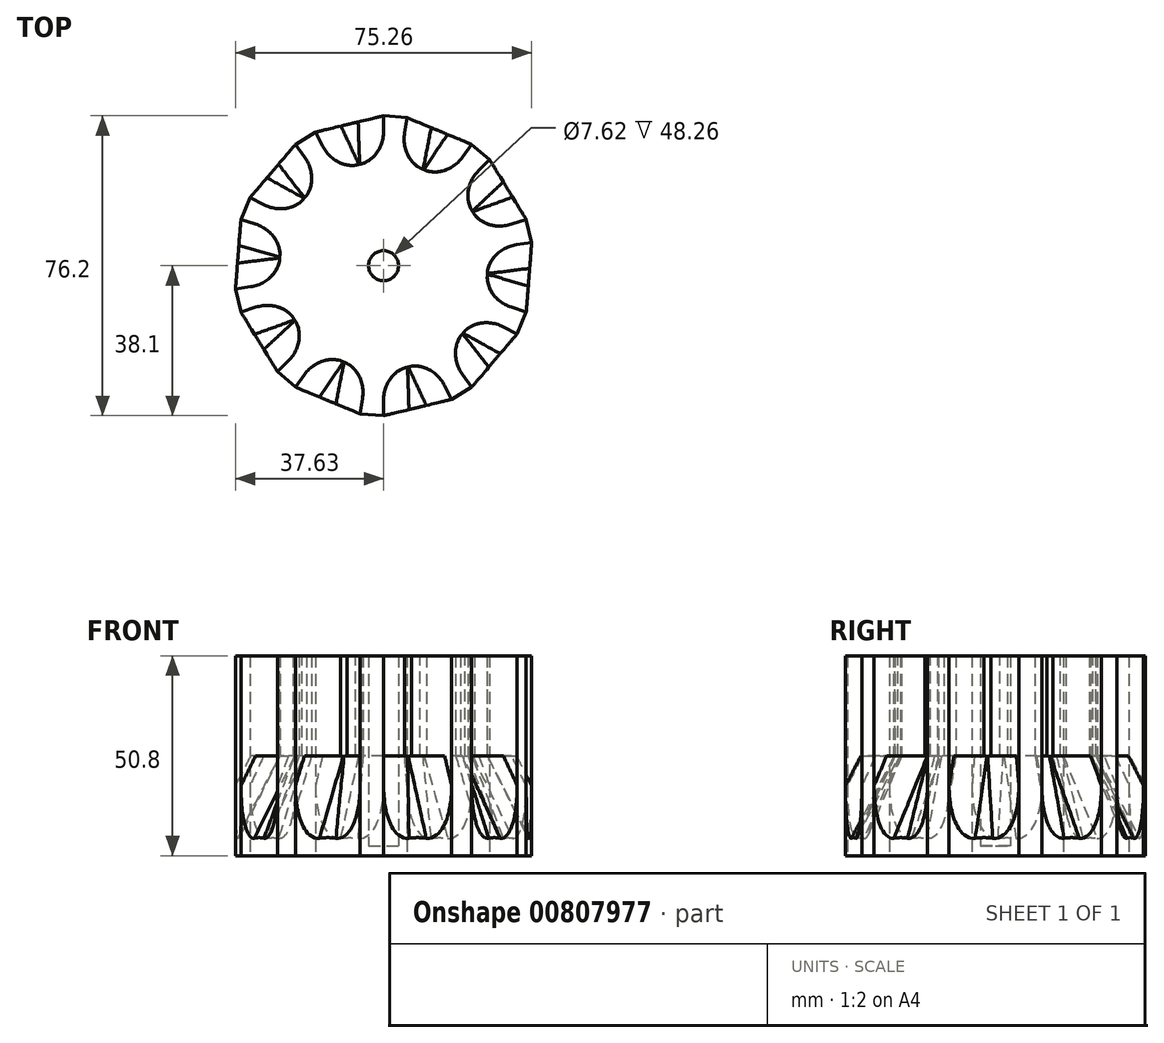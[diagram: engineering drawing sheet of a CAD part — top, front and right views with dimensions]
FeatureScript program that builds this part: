
annotation { "Feature Type Name" : "Feature", "Feature Type Description" : "" }
export const myFeature = defineFeature(function(context is Context, id is Id, definition is map)
    precondition{}
    {
        {
            var Q0;
            Q0=qCreatedBy(makeId("Top.planeOp"),FACE);
            var sketch = newSketch(context, id + "F0", { "sketchPlane" : qUnion([Q0])});
            skCircle(sketch, "E0", {"center": v(0, 0) * mm, "radius": 38.1 * mm});
            skLineSegment(sketch, "E1", {"start": v(0, -27.25) * mm, "end": v(0, -38.1) * mm});
            skLineSegment(sketch, "E2", {"start": v(0, -38.1) * mm, "end": v(17.29, -33.95) * mm});
            skLineSegment(sketch, "E3", {"start": v(17.29, -33.95) * mm, "end": v(12.33, -24.22) * mm});
            skLineSegment(sketch, "E4", {"start": v(0, -27.25) * mm, "end": v(12.33, -24.22) * mm});
            skLineSegment(sketch, "E5.1.0", {"start": v(33.94, -17.3) * mm, "end": v(24.21, -12.34) * mm});
            skLineSegment(sketch, "E5.1.1", {"start": v(16.02, -22.04) * mm, "end": v(24.21, -12.34) * mm});
            skLineSegment(sketch, "E5.1.2", {"start": v(16.02, -22.04) * mm, "end": v(22.4, -30.82) * mm});
            skLineSegment(sketch, "E5.1.3", {"start": v(22.4, -30.82) * mm, "end": v(33.94, -17.3) * mm});
            skLineSegment(sketch, "E5.2.0", {"start": v(37.63, 5.95) * mm, "end": v(26.85, 4.25) * mm});
            skLineSegment(sketch, "E5.2.1", {"start": v(25.91, -8.42) * mm, "end": v(26.85, 4.25) * mm});
            skLineSegment(sketch, "E5.2.2", {"start": v(25.91, -8.42) * mm, "end": v(36.24, -11.77) * mm});
            skLineSegment(sketch, "E5.2.3", {"start": v(36.24, -11.77) * mm, "end": v(37.63, 5.95) * mm});
            skLineSegment(sketch, "E5.3.0", {"start": v(26.95, 26.93) * mm, "end": v(19.22, 19.21) * mm});
            skLineSegment(sketch, "E5.3.1", {"start": v(25.91, 8.42) * mm, "end": v(19.22, 19.21) * mm});
            skLineSegment(sketch, "E5.3.2", {"start": v(25.91, 8.42) * mm, "end": v(36.24, 11.77) * mm});
            skLineSegment(sketch, "E5.3.3", {"start": v(36.24, 11.77) * mm, "end": v(26.95, 26.93) * mm});
            skLineSegment(sketch, "E5.4.0", {"start": v(5.97, 37.63) * mm, "end": v(4.26, 26.84) * mm});
            skLineSegment(sketch, "E5.4.1", {"start": v(16.02, 22.04) * mm, "end": v(4.26, 26.84) * mm});
            skLineSegment(sketch, "E5.4.2", {"start": v(16.02, 22.04) * mm, "end": v(22.4, 30.82) * mm});
            skLineSegment(sketch, "E5.4.3", {"start": v(22.4, 30.82) * mm, "end": v(5.97, 37.63) * mm});
            skLineSegment(sketch, "E5.5.0", {"start": v(-17.29, 33.95) * mm, "end": v(-12.33, 24.22) * mm});
            skLineSegment(sketch, "E5.5.1", {"start": v(0, 27.25) * mm, "end": v(-12.33, 24.22) * mm});
            skLineSegment(sketch, "E5.5.2", {"start": v(0, 27.25) * mm, "end": v(0, 38.1) * mm});
            skLineSegment(sketch, "E5.5.3", {"start": v(0, 38.1) * mm, "end": v(-17.29, 33.95) * mm});
            skLineSegment(sketch, "E6.1.6.0", {"start": v(-33.94, 17.3) * mm, "end": v(-24.21, 12.34) * mm});
            skLineSegment(sketch, "E6.3.6.0", {"start": v(-16.02, 22.04) * mm, "end": v(-24.21, 12.34) * mm});
            skLineSegment(sketch, "E6.6.6.0", {"start": v(-16.02, 22.04) * mm, "end": v(-22.4, 30.82) * mm});
            skLineSegment(sketch, "E6.9.6.0", {"start": v(-22.4, 30.82) * mm, "end": v(-33.94, 17.3) * mm});
            skLineSegment(sketch, "E6.1.7.0", {"start": v(-37.63, -5.95) * mm, "end": v(-26.85, -4.25) * mm});
            skLineSegment(sketch, "E6.3.7.0", {"start": v(-25.91, 8.42) * mm, "end": v(-26.85, -4.25) * mm});
            skLineSegment(sketch, "E6.6.7.0", {"start": v(-25.91, 8.42) * mm, "end": v(-36.24, 11.77) * mm});
            skLineSegment(sketch, "E6.9.7.0", {"start": v(-36.24, 11.77) * mm, "end": v(-37.63, -5.95) * mm});
            skLineSegment(sketch, "E6.1.8.0", {"start": v(-26.95, -26.93) * mm, "end": v(-19.22, -19.21) * mm});
            skLineSegment(sketch, "E6.3.8.0", {"start": v(-25.91, -8.42) * mm, "end": v(-19.22, -19.21) * mm});
            skLineSegment(sketch, "E6.6.8.0", {"start": v(-25.91, -8.42) * mm, "end": v(-36.24, -11.77) * mm});
            skLineSegment(sketch, "E6.9.8.0", {"start": v(-36.24, -11.77) * mm, "end": v(-26.95, -26.93) * mm});
            skLineSegment(sketch, "E6.1.9.0", {"start": v(-5.97, -37.63) * mm, "end": v(-4.26, -26.84) * mm});
            skLineSegment(sketch, "E6.3.9.0", {"start": v(-16.02, -22.04) * mm, "end": v(-4.26, -26.84) * mm});
            skLineSegment(sketch, "E6.6.9.0", {"start": v(-16.02, -22.04) * mm, "end": v(-22.4, -30.82) * mm});
            skLineSegment(sketch, "E6.9.9.0", {"start": v(-22.4, -30.82) * mm, "end": v(-5.97, -37.63) * mm});
            skCircle(sketch, "E7", {"center": v(0, 0) * mm, "radius": 3.81 * mm});
            skSolve(sketch);
        }
        {
            var Q0;
            {var subQ7=sQuery(id+"F0.wireOp",EDGE,"E1");Q0=makeQuery(id+"F0.imprint","IMPRINT",FACE,{"disambiguationData":[TD([[makeQuery(id+"F0.imprint","IMPRINT",EDGE,{"derivedFrom":subQ7}),-1.0]])]});}
            extrude(context, id + "F1", {"entities" : qUnion([Q0]), "depth" : 25.4 * mm, "offsetDistance" : 25.4 * mm});
        }
        {
            var Q0;
            Q0=makeQuery(id+"F1.opExtrude","CAP_FACE",FACE,{"disambiguationData":[OSD([sQuery(id+"F0.wireOp",EDGE,"E0"),sQuery(id+"F0.wireOp",EDGE,"E1"),sQuery(id+"F0.wireOp",EDGE,"E3"),sQuery(id+"F0.wireOp",EDGE,"E4"),sQuery(id+"F0.wireOp",EDGE,"E5.1.0"),sQuery(id+"F0.wireOp",EDGE,"E5.1.1"),sQuery(id+"F0.wireOp",EDGE,"E5.1.2"),sQuery(id+"F0.wireOp",EDGE,"E5.2.0"),sQuery(id+"F0.wireOp",EDGE,"E5.2.1"),sQuery(id+"F0.wireOp",EDGE,"E5.2.2"),sQuery(id+"F0.wireOp",EDGE,"E5.3.0"),sQuery(id+"F0.wireOp",EDGE,"E5.3.1"),sQuery(id+"F0.wireOp",EDGE,"E5.3.2"),sQuery(id+"F0.wireOp",EDGE,"E5.4.0"),sQuery(id+"F0.wireOp",EDGE,"E5.4.1"),sQuery(id+"F0.wireOp",EDGE,"E5.4.2"),sQuery(id+"F0.wireOp",EDGE,"E5.5.0"),sQuery(id+"F0.wireOp",EDGE,"E5.5.1"),sQuery(id+"F0.wireOp",EDGE,"E5.5.2"),sQuery(id+"F0.wireOp",EDGE,"E6.1.6.0"),sQuery(id+"F0.wireOp",EDGE,"E6.3.6.0"),sQuery(id+"F0.wireOp",EDGE,"E6.6.6.0"),sQuery(id+"F0.wireOp",EDGE,"E6.1.7.0"),sQuery(id+"F0.wireOp",EDGE,"E6.3.7.0"),sQuery(id+"F0.wireOp",EDGE,"E6.6.7.0"),sQuery(id+"F0.wireOp",EDGE,"E6.1.8.0"),sQuery(id+"F0.wireOp",EDGE,"E6.3.8.0"),sQuery(id+"F0.wireOp",EDGE,"E6.6.8.0"),sQuery(id+"F0.wireOp",EDGE,"E6.1.9.0"),sQuery(id+"F0.wireOp",EDGE,"E6.3.9.0"),sQuery(id+"F0.wireOp",EDGE,"E6.6.9.0")])],"isStart":true});
            var sketch = newSketch(context, id + "F2", { "sketchPlane" : qUnion([Q0])});
            skCircle(sketch, "E8", {"center": v(0, 0) * mm, "radius": 38.1 * mm});
            skLineSegment(sketch, "E9", {"start": v(36.24, -11.77) * mm, "end": v(26.95, -26.93) * mm});
            skLineSegment(sketch, "E10.1.0", {"start": v(36.24, 11.77) * mm, "end": v(37.63, -5.95) * mm});
            skLineSegment(sketch, "E10.2.0", {"start": v(22.4, 30.82) * mm, "end": v(33.94, 17.3) * mm});
            skLineSegment(sketch, "E10.3.0", {"start": v(0, 38.1) * mm, "end": v(17.29, 33.95) * mm});
            skLineSegment(sketch, "E10.4.0", {"start": v(-22.4, 30.82) * mm, "end": v(-5.97, 37.63) * mm});
            skLineSegment(sketch, "E10.5.0", {"start": v(-36.24, 11.77) * mm, "end": v(-26.95, 26.93) * mm});
            skLineSegment(sketch, "E10.6.0", {"start": v(-36.24, -11.77) * mm, "end": v(-37.63, 5.95) * mm});
            skLineSegment(sketch, "E10.7.0", {"start": v(-22.4, -30.82) * mm, "end": v(-33.94, -17.3) * mm});
            skLineSegment(sketch, "E10.8.0", {"start": v(0, -38.1) * mm, "end": v(-17.29, -33.95) * mm});
            skLineSegment(sketch, "E10.9.0", {"start": v(22.4, -30.82) * mm, "end": v(5.97, -37.63) * mm});
            skSolve(sketch);
        }
        {
            var Q0;
            Q0 = qSketchRegion(id + "F2", true);
            extrude(context, id + "F3", {"entities" : qUnion([Q0]), "operationType" : NewBodyOperationType.ADD, "oppositeDirection" : true, "depth" : 2.54 * mm, "offsetDistance" : 25.4 * mm});
        }
        {
            var Q0;
            Q0=qCreatedBy(makeId("Front.planeOp"),FACE);
            var sketch = newSketch(context, id + "F4", { "sketchPlane" : qUnion([Q0])});
            skLineSegment(sketch, "E11", {"start": v(0, 0) * mm, "end": v(0, 29.85) * mm});
            skSolve(sketch);
        }
        {
            var Q0;
            Q0=makeQuery(id+"F1.opExtrude","CAP_EDGE",EDGE,{"disambiguationData":[OSD([sQuery(id+"F0.wireOp",EDGE,"E5.1.1")])],"isStart":false});
            cPoint(context, id + "F5", {"entities" : qUnion([Q0]), "parameter" : 0.5});
        }
        {
            var Q0;
            Q0=makeQuery(id+"F3.boolean.opBoolean","INTERSECT",EDGE,{"derivedFrom":[makeQuery(id+"F1.opExtrude","SWEPT_FACE",FACE,{"disambiguationData":[OSD([sQuery(id+"F0.wireOp",EDGE,"E5.1.1")])]}),makeQuery(id+"F3.opExtrude","CAP_FACE",FACE,{"disambiguationData":[OSD([sQuery(id+"F2.wireOp",EDGE,"E8")])],"isStart":false})]});
            cPoint(context, id + "F6", {"entities" : qUnion([Q0]), "parameter" : 0.5});
        }
        {
            var Q0;
            {var subQ8=sQuery(id+"F2.wireOp",EDGE,"E8");var subQ9=sQuery(id+"F0.wireOp",EDGE,"E5.1.0");Q0=makeQuery(id+"F3.boolean.opBoolean","SPLIT",EDGE,{"disambiguationData":[TD([makeQuery(id+"F1.opExtrude","SWEPT_FACE",FACE,{"disambiguationData":[OSD([subQ9])]})])],"derivedFrom":makeQuery(id+"F3.opExtrude","CAP_EDGE",EDGE,{"disambiguationData":[OSD([subQ8])],"isStart":false})});}
            cPoint(context, id + "F7", {"entities" : qUnion([Q0]), "parameter" : 0.5});
        }
        {
            var Q0;
            Q0 = qCreatedBy(id + "F5" ,VERTEX);
            var Q1;
            Q1 = qCreatedBy(id + "F6" ,VERTEX);
            var Q2;
            Q2 = qCreatedBy(id + "F7" ,VERTEX);
            cPlane(context, id + "F8", {"entities" : qUnion([Q0, Q1, Q2]), "cplaneType" : CPlaneType.THREE_POINT, "offset" : 25.4 * mm, "width" : 152.4 * mm, "height" : 152.4 * mm});
        }
        {
            var Q0;
            Q0=qCreatedBy(id+"F8.planeOp",FACE);
            var sketch = newSketch(context, id + "F9", { "sketchPlane" : qUnion([Q0])});
            skLineSegment(sketch, "E12.0.0", {"start": v(-26.5, 2.54) * mm, "end": v(-26.43, 2.54) * mm});
            skLineSegment(sketch, "E12.0.1", {"start": v(-26.43, 2.54) * mm, "end": v(-26.43, 25.4) * mm});
            skLineSegment(sketch, "E12.0.2", {"start": v(-26.43, 25.4) * mm, "end": v(-26.5, 25.4) * mm});
            skLineSegment(sketch, "E12.0.3", {"start": v(-26.5, 25.4) * mm, "end": v(-26.5, 2.54) * mm});
            skLineSegment(sketch, "E13.0.0", {"start": v(-26.5, 2.54) * mm, "end": v(-37.04, 2.54) * mm});
            skLineSegment(sketch, "E13.0.1", {"start": v(-37.04, 2.54) * mm, "end": v(-38.1, 2.54) * mm});
            skLineSegment(sketch, "E13.0.2", {"start": v(-37.05, 2.54) * mm, "end": v(-26.43, 2.54) * mm});
            skLineSegment(sketch, "E13.0.3", {"start": v(-26.43, 2.54) * mm, "end": v(-26.5, 2.54) * mm});
            skLineSegment(sketch, "E14", {"start": v(-26.43, 25.4) * mm, "end": v(-38.1, 2.54) * mm});
            skFitSpline(sketch, "E15", {"points": [v(-26.43, 25.4) * mm, v(-33.43, 4) * mm, v(-38.1, 2.54) * mm], "startDerivative": vector(-8.76, -40.49) * mm, "endDerivative": vector(-15.38, -0.36) * mm});
            skSolve(sketch);
        }
        {
            var Q0;
            Q0 = qSketchRegion(id + "F9", true);
            var Q1;
            Q1=sQuery(id+"F4.wireOp",EDGE,"E11");
            revolve(context, id + "F10", {"operationType" : NewBodyOperationType.ADD, "surfaceOperationType" : NewSurfaceOperationType.NEW, "entities" : qUnion([Q0]), "axis" : qUnion([Q1]), "revolveType" : RevolveType.FULL});
        }
        {
            var Q0;
            Q0=makeQuery(id+"F3.boolean.opBoolean","MERGE",FACE,{"derivedFrom":[makeQuery(id+"F1.opExtrude","CAP_FACE",FACE,{"disambiguationData":[OSD([sQuery(id+"F0.wireOp",EDGE,"E0"),sQuery(id+"F0.wireOp",EDGE,"E1"),sQuery(id+"F0.wireOp",EDGE,"E3"),sQuery(id+"F0.wireOp",EDGE,"E4"),sQuery(id+"F0.wireOp",EDGE,"E5.1.0"),sQuery(id+"F0.wireOp",EDGE,"E5.1.1"),sQuery(id+"F0.wireOp",EDGE,"E5.1.2"),sQuery(id+"F0.wireOp",EDGE,"E5.2.0"),sQuery(id+"F0.wireOp",EDGE,"E5.2.1"),sQuery(id+"F0.wireOp",EDGE,"E5.2.2"),sQuery(id+"F0.wireOp",EDGE,"E5.3.0"),sQuery(id+"F0.wireOp",EDGE,"E5.3.1"),sQuery(id+"F0.wireOp",EDGE,"E5.3.2"),sQuery(id+"F0.wireOp",EDGE,"E5.4.0"),sQuery(id+"F0.wireOp",EDGE,"E5.4.1"),sQuery(id+"F0.wireOp",EDGE,"E5.4.2"),sQuery(id+"F0.wireOp",EDGE,"E5.5.0"),sQuery(id+"F0.wireOp",EDGE,"E5.5.1"),sQuery(id+"F0.wireOp",EDGE,"E5.5.2"),sQuery(id+"F0.wireOp",EDGE,"E6.1.6.0"),sQuery(id+"F0.wireOp",EDGE,"E6.3.6.0"),sQuery(id+"F0.wireOp",EDGE,"E6.6.6.0"),sQuery(id+"F0.wireOp",EDGE,"E6.1.7.0"),sQuery(id+"F0.wireOp",EDGE,"E6.3.7.0"),sQuery(id+"F0.wireOp",EDGE,"E6.6.7.0"),sQuery(id+"F0.wireOp",EDGE,"E6.1.8.0"),sQuery(id+"F0.wireOp",EDGE,"E6.3.8.0"),sQuery(id+"F0.wireOp",EDGE,"E6.6.8.0"),sQuery(id+"F0.wireOp",EDGE,"E6.1.9.0"),sQuery(id+"F0.wireOp",EDGE,"E6.3.9.0"),sQuery(id+"F0.wireOp",EDGE,"E6.6.9.0"),sQuery(id+"F0.wireOp",EDGE,"E7")])],"isStart":true}),makeQuery(id+"F3.opExtrude","CAP_FACE",FACE,{"disambiguationData":[OSD([sQuery(id+"F2.wireOp",EDGE,"E8")])],"isStart":true})]});
            var sketch = newSketch(context, id + "F11", { "sketchPlane" : qUnion([Q0])});
            skPoint(sketch, "E16.0", {"position": v(37.63, -5.95) * mm});
            skPoint(sketch, "E17.0", {"position": v(36.24, -11.77) * mm});
            skPoint(sketch, "E18.0", {"position": v(26.95, -26.93) * mm});
            skLineSegment(sketch, "E19", {"start": v(37.63, -5.95) * mm, "end": v(36.24, -11.77) * mm});
            skLineSegment(sketch, "E20", {"start": v(26.95, -26.93) * mm, "end": v(36.24, -11.77) * mm});
            skLineSegment(sketch, "E21.1.0", {"start": v(33.94, 17.3) * mm, "end": v(36.24, 11.77) * mm});
            skLineSegment(sketch, "E21.1.1", {"start": v(37.63, -5.95) * mm, "end": v(36.24, 11.77) * mm});
            skLineSegment(sketch, "E21.2.0", {"start": v(17.29, 33.95) * mm, "end": v(22.4, 30.82) * mm});
            skLineSegment(sketch, "E21.2.1", {"start": v(33.94, 17.3) * mm, "end": v(22.4, 30.82) * mm});
            skLineSegment(sketch, "E21.3.0", {"start": v(-5.97, 37.63) * mm, "end": v(0, 38.1) * mm});
            skLineSegment(sketch, "E21.3.1", {"start": v(17.29, 33.95) * mm, "end": v(0, 38.1) * mm});
            skLineSegment(sketch, "E21.4.0", {"start": v(-26.95, 26.93) * mm, "end": v(-22.4, 30.82) * mm});
            skLineSegment(sketch, "E21.4.1", {"start": v(-5.97, 37.63) * mm, "end": v(-22.4, 30.82) * mm});
            skLineSegment(sketch, "E21.5.0", {"start": v(-37.63, 5.95) * mm, "end": v(-36.24, 11.77) * mm});
            skLineSegment(sketch, "E21.5.1", {"start": v(-26.95, 26.93) * mm, "end": v(-36.24, 11.77) * mm});
            skLineSegment(sketch, "E21.6.0", {"start": v(-33.94, -17.3) * mm, "end": v(-36.24, -11.77) * mm});
            skLineSegment(sketch, "E21.6.1", {"start": v(-37.63, 5.95) * mm, "end": v(-36.24, -11.77) * mm});
            skLineSegment(sketch, "E21.7.0", {"start": v(-17.29, -33.95) * mm, "end": v(-22.4, -30.82) * mm});
            skLineSegment(sketch, "E21.7.1", {"start": v(-33.94, -17.3) * mm, "end": v(-22.4, -30.82) * mm});
            skLineSegment(sketch, "E21.8.0", {"start": v(5.97, -37.63) * mm, "end": v(0, -38.1) * mm});
            skLineSegment(sketch, "E21.8.1", {"start": v(-17.29, -33.95) * mm, "end": v(0, -38.1) * mm});
            skLineSegment(sketch, "E21.9.0", {"start": v(26.95, -26.93) * mm, "end": v(22.4, -30.82) * mm});
            skLineSegment(sketch, "E21.9.1", {"start": v(5.97, -37.63) * mm, "end": v(22.4, -30.82) * mm});
            skPoint(sketch, "E21.center", {"position": v(0, 0) * mm});
            skSolve(sketch);
        }
        {
            var Q0;
            {var subQ0=sQuery(id+"F11.wireOp",EDGE,"E21.9.1");Q0=makeQuery(id+"F11.imprint","IMPRINT",FACE,{"disambiguationData":[TD([[makeQuery(id+"F11.imprint","IMPRINT",EDGE,{"derivedFrom":subQ0}),-1.0]])]});}
            var Q1;
            {var subQ0=sQuery(id+"F11.wireOp",EDGE,"E21.9.0");Q1=makeQuery(id+"F11.imprint","IMPRINT",FACE,{"disambiguationData":[TD([[makeQuery(id+"F11.imprint","IMPRINT",EDGE,{"derivedFrom":subQ0}),1.0]])]});}
            var Q2;
            {var subQ0=sQuery(id+"F11.wireOp",EDGE,"E20");Q2=makeQuery(id+"F11.imprint","IMPRINT",FACE,{"disambiguationData":[TD([[makeQuery(id+"F11.imprint","IMPRINT",EDGE,{"derivedFrom":subQ0}),-1.0]])]});}
            var Q3;
            {var subQ0=sQuery(id+"F11.wireOp",EDGE,"E19");Q3=makeQuery(id+"F11.imprint","IMPRINT",FACE,{"disambiguationData":[TD([[makeQuery(id+"F11.imprint","IMPRINT",EDGE,{"derivedFrom":subQ0}),1.0]])]});}
            var Q4;
            {var subQ0=sQuery(id+"F11.wireOp",EDGE,"E21.1.1");Q4=makeQuery(id+"F11.imprint","IMPRINT",FACE,{"disambiguationData":[TD([[makeQuery(id+"F11.imprint","IMPRINT",EDGE,{"derivedFrom":subQ0}),-1.0]])]});}
            var Q5;
            {var subQ0=sQuery(id+"F11.wireOp",EDGE,"E21.1.0");Q5=makeQuery(id+"F11.imprint","IMPRINT",FACE,{"disambiguationData":[TD([[makeQuery(id+"F11.imprint","IMPRINT",EDGE,{"derivedFrom":subQ0}),1.0]])]});}
            var Q6;
            {var subQ0=sQuery(id+"F11.wireOp",EDGE,"E21.2.1");Q6=makeQuery(id+"F11.imprint","IMPRINT",FACE,{"disambiguationData":[TD([[makeQuery(id+"F11.imprint","IMPRINT",EDGE,{"derivedFrom":subQ0}),-1.0]])]});}
            var Q7;
            {var subQ0=sQuery(id+"F11.wireOp",EDGE,"E21.2.0");Q7=makeQuery(id+"F11.imprint","IMPRINT",FACE,{"disambiguationData":[TD([[makeQuery(id+"F11.imprint","IMPRINT",EDGE,{"derivedFrom":subQ0}),1.0]])]});}
            var Q8;
            {var subQ0=sQuery(id+"F11.wireOp",EDGE,"E21.3.1");Q8=makeQuery(id+"F11.imprint","IMPRINT",FACE,{"disambiguationData":[TD([[makeQuery(id+"F11.imprint","IMPRINT",EDGE,{"derivedFrom":subQ0}),-1.0]])]});}
            var Q9;
            {var subQ0=sQuery(id+"F11.wireOp",EDGE,"E21.3.0");Q9=makeQuery(id+"F11.imprint","IMPRINT",FACE,{"disambiguationData":[TD([[makeQuery(id+"F11.imprint","IMPRINT",EDGE,{"derivedFrom":subQ0}),1.0]])]});}
            var Q10;
            {var subQ0=sQuery(id+"F11.wireOp",EDGE,"E21.4.1");Q10=makeQuery(id+"F11.imprint","IMPRINT",FACE,{"disambiguationData":[TD([[makeQuery(id+"F11.imprint","IMPRINT",EDGE,{"derivedFrom":subQ0}),-1.0]])]});}
            var Q11;
            {var subQ0=sQuery(id+"F11.wireOp",EDGE,"E21.4.0");Q11=makeQuery(id+"F11.imprint","IMPRINT",FACE,{"disambiguationData":[TD([[makeQuery(id+"F11.imprint","IMPRINT",EDGE,{"derivedFrom":subQ0}),1.0]])]});}
            var Q12;
            {var subQ0=sQuery(id+"F11.wireOp",EDGE,"E21.5.1");Q12=makeQuery(id+"F11.imprint","IMPRINT",FACE,{"disambiguationData":[TD([[makeQuery(id+"F11.imprint","IMPRINT",EDGE,{"derivedFrom":subQ0}),-1.0]])]});}
            var Q13;
            {var subQ0=sQuery(id+"F11.wireOp",EDGE,"E21.5.0");Q13=makeQuery(id+"F11.imprint","IMPRINT",FACE,{"disambiguationData":[TD([[makeQuery(id+"F11.imprint","IMPRINT",EDGE,{"derivedFrom":subQ0}),1.0]])]});}
            var Q14;
            {var subQ0=sQuery(id+"F11.wireOp",EDGE,"E21.6.1");Q14=makeQuery(id+"F11.imprint","IMPRINT",FACE,{"disambiguationData":[TD([[makeQuery(id+"F11.imprint","IMPRINT",EDGE,{"derivedFrom":subQ0}),-1.0]])]});}
            var Q15;
            {var subQ0=sQuery(id+"F11.wireOp",EDGE,"E21.6.0");Q15=makeQuery(id+"F11.imprint","IMPRINT",FACE,{"disambiguationData":[TD([[makeQuery(id+"F11.imprint","IMPRINT",EDGE,{"derivedFrom":subQ0}),1.0]])]});}
            var Q16;
            {var subQ0=sQuery(id+"F11.wireOp",EDGE,"E21.7.1");Q16=makeQuery(id+"F11.imprint","IMPRINT",FACE,{"disambiguationData":[TD([[makeQuery(id+"F11.imprint","IMPRINT",EDGE,{"derivedFrom":subQ0}),-1.0]])]});}
            var Q17;
            {var subQ0=sQuery(id+"F11.wireOp",EDGE,"E21.7.0");Q17=makeQuery(id+"F11.imprint","IMPRINT",FACE,{"disambiguationData":[TD([[makeQuery(id+"F11.imprint","IMPRINT",EDGE,{"derivedFrom":subQ0}),1.0]])]});}
            var Q18;
            {var subQ0=sQuery(id+"F11.wireOp",EDGE,"E21.8.1");Q18=makeQuery(id+"F11.imprint","IMPRINT",FACE,{"disambiguationData":[TD([[makeQuery(id+"F11.imprint","IMPRINT",EDGE,{"derivedFrom":subQ0}),-1.0]])]});}
            var Q19;
            {var subQ0=sQuery(id+"F11.wireOp",EDGE,"E21.8.0");Q19=makeQuery(id+"F11.imprint","IMPRINT",FACE,{"disambiguationData":[TD([[makeQuery(id+"F11.imprint","IMPRINT",EDGE,{"derivedFrom":subQ0}),1.0]])]});}
            extrude(context, id + "F12", {"entities" : qUnion([Q0, Q1, Q2, Q3, Q4, Q5, Q6, Q7, Q8, Q9, Q10, Q11, Q12, Q13, Q14, Q15, Q16, Q17, Q18, Q19]), "operationType" : NewBodyOperationType.REMOVE, "oppositeDirection" : true, "depth" : 25.4 * mm, "offsetDistance" : 25.4 * mm});
        }
        {
            var Q0;
            Q0=makeQuery(id+"F10.boolean.opBoolean","INTERSECT",EDGE,{"derivedFrom":[makeQuery(id+"F1.opExtrude","SWEPT_FACE",FACE,{"disambiguationData":[OSD([sQuery(id+"F0.wireOp",EDGE,"E6.6.7.0")])]}),makeQuery(id+"F10.opRevolve","SWEPT_FACE",FACE,{"disambiguationData":[OSD([sQuery(id+"F9.wireOp",EDGE,"E14")])]})]});
            var Q1;
            Q1=makeQuery(id+"F10.boolean.opBoolean","INTERSECT",EDGE,{"derivedFrom":[makeQuery(id+"F1.opExtrude","SWEPT_FACE",FACE,{"disambiguationData":[OSD([sQuery(id+"F0.wireOp",EDGE,"E6.1.7.0")])]}),makeQuery(id+"F10.opRevolve","SWEPT_FACE",FACE,{"disambiguationData":[OSD([sQuery(id+"F9.wireOp",EDGE,"E14")])]})]});
            var Q2;
            Q2=makeQuery(id+"F10.boolean.opBoolean","INTERSECT",EDGE,{"derivedFrom":[makeQuery(id+"F1.opExtrude","SWEPT_FACE",FACE,{"disambiguationData":[OSD([sQuery(id+"F0.wireOp",EDGE,"E6.6.8.0")])]}),makeQuery(id+"F10.opRevolve","SWEPT_FACE",FACE,{"disambiguationData":[OSD([sQuery(id+"F9.wireOp",EDGE,"E14")])]})]});
            var Q3;
            Q3=makeQuery(id+"F10.boolean.opBoolean","INTERSECT",EDGE,{"derivedFrom":[makeQuery(id+"F1.opExtrude","SWEPT_FACE",FACE,{"disambiguationData":[OSD([sQuery(id+"F0.wireOp",EDGE,"E6.1.8.0")])]}),makeQuery(id+"F10.opRevolve","SWEPT_FACE",FACE,{"disambiguationData":[OSD([sQuery(id+"F9.wireOp",EDGE,"E14")])]})]});
            var Q4;
            Q4=makeQuery(id+"F10.boolean.opBoolean","INTERSECT",EDGE,{"derivedFrom":[makeQuery(id+"F1.opExtrude","SWEPT_FACE",FACE,{"disambiguationData":[OSD([sQuery(id+"F0.wireOp",EDGE,"E6.1.9.0")])]}),makeQuery(id+"F10.opRevolve","SWEPT_FACE",FACE,{"disambiguationData":[OSD([sQuery(id+"F9.wireOp",EDGE,"E14")])]})]});
            var Q5;
            Q5=makeQuery(id+"F10.boolean.opBoolean","INTERSECT",EDGE,{"derivedFrom":[makeQuery(id+"F1.opExtrude","SWEPT_FACE",FACE,{"disambiguationData":[OSD([sQuery(id+"F0.wireOp",EDGE,"E6.6.9.0")])]}),makeQuery(id+"F10.opRevolve","SWEPT_FACE",FACE,{"disambiguationData":[OSD([sQuery(id+"F9.wireOp",EDGE,"E14")])]})]});
            var Q6;
            Q6=makeQuery(id+"F10.boolean.opBoolean","INTERSECT",EDGE,{"derivedFrom":[makeQuery(id+"F1.opExtrude","SWEPT_FACE",FACE,{"disambiguationData":[OSD([sQuery(id+"F0.wireOp",EDGE,"E3")])]}),makeQuery(id+"F10.opRevolve","SWEPT_FACE",FACE,{"disambiguationData":[OSD([sQuery(id+"F9.wireOp",EDGE,"E14")])]})]});
            var Q7;
            Q7=makeQuery(id+"F10.boolean.opBoolean","INTERSECT",EDGE,{"derivedFrom":[makeQuery(id+"F1.opExtrude","SWEPT_FACE",FACE,{"disambiguationData":[OSD([sQuery(id+"F0.wireOp",EDGE,"E1")])]}),makeQuery(id+"F10.opRevolve","SWEPT_FACE",FACE,{"disambiguationData":[OSD([sQuery(id+"F9.wireOp",EDGE,"E14")])]})]});
            var Q8;
            Q8=makeQuery(id+"F10.boolean.opBoolean","INTERSECT",EDGE,{"derivedFrom":[makeQuery(id+"F1.opExtrude","SWEPT_FACE",FACE,{"disambiguationData":[OSD([sQuery(id+"F0.wireOp",EDGE,"E5.1.0")])]}),makeQuery(id+"F10.opRevolve","SWEPT_FACE",FACE,{"disambiguationData":[OSD([sQuery(id+"F9.wireOp",EDGE,"E14")])]})]});
            var Q9;
            Q9=makeQuery(id+"F10.boolean.opBoolean","INTERSECT",EDGE,{"derivedFrom":[makeQuery(id+"F1.opExtrude","SWEPT_FACE",FACE,{"disambiguationData":[OSD([sQuery(id+"F0.wireOp",EDGE,"E5.1.2")])]}),makeQuery(id+"F10.opRevolve","SWEPT_FACE",FACE,{"disambiguationData":[OSD([sQuery(id+"F9.wireOp",EDGE,"E14")])]})]});
            var Q10;
            Q10=makeQuery(id+"F10.boolean.opBoolean","INTERSECT",EDGE,{"derivedFrom":[makeQuery(id+"F1.opExtrude","SWEPT_FACE",FACE,{"disambiguationData":[OSD([sQuery(id+"F0.wireOp",EDGE,"E5.2.0")])]}),makeQuery(id+"F10.opRevolve","SWEPT_FACE",FACE,{"disambiguationData":[OSD([sQuery(id+"F9.wireOp",EDGE,"E14")])]})]});
            var Q11;
            Q11=makeQuery(id+"F10.boolean.opBoolean","INTERSECT",EDGE,{"derivedFrom":[makeQuery(id+"F1.opExtrude","SWEPT_FACE",FACE,{"disambiguationData":[OSD([sQuery(id+"F0.wireOp",EDGE,"E5.2.2")])]}),makeQuery(id+"F10.opRevolve","SWEPT_FACE",FACE,{"disambiguationData":[OSD([sQuery(id+"F9.wireOp",EDGE,"E14")])]})]});
            var Q12;
            Q12=makeQuery(id+"F10.boolean.opBoolean","INTERSECT",EDGE,{"derivedFrom":[makeQuery(id+"F1.opExtrude","SWEPT_FACE",FACE,{"disambiguationData":[OSD([sQuery(id+"F0.wireOp",EDGE,"E5.3.2")])]}),makeQuery(id+"F10.opRevolve","SWEPT_FACE",FACE,{"disambiguationData":[OSD([sQuery(id+"F9.wireOp",EDGE,"E14")])]})]});
            var Q13;
            Q13=makeQuery(id+"F10.boolean.opBoolean","INTERSECT",EDGE,{"derivedFrom":[makeQuery(id+"F1.opExtrude","SWEPT_FACE",FACE,{"disambiguationData":[OSD([sQuery(id+"F0.wireOp",EDGE,"E5.3.0")])]}),makeQuery(id+"F10.opRevolve","SWEPT_FACE",FACE,{"disambiguationData":[OSD([sQuery(id+"F9.wireOp",EDGE,"E14")])]})]});
            var Q14;
            Q14=makeQuery(id+"F10.boolean.opBoolean","INTERSECT",EDGE,{"derivedFrom":[makeQuery(id+"F1.opExtrude","SWEPT_FACE",FACE,{"disambiguationData":[OSD([sQuery(id+"F0.wireOp",EDGE,"E6.1.6.0")])]}),makeQuery(id+"F10.opRevolve","SWEPT_FACE",FACE,{"disambiguationData":[OSD([sQuery(id+"F9.wireOp",EDGE,"E14")])]})]});
            var Q15;
            Q15=makeQuery(id+"F10.boolean.opBoolean","INTERSECT",EDGE,{"derivedFrom":[makeQuery(id+"F1.opExtrude","SWEPT_FACE",FACE,{"disambiguationData":[OSD([sQuery(id+"F0.wireOp",EDGE,"E5.5.2")])]}),makeQuery(id+"F10.opRevolve","SWEPT_FACE",FACE,{"disambiguationData":[OSD([sQuery(id+"F9.wireOp",EDGE,"E14")])]})]});
            var Q16;
            Q16=makeQuery(id+"F10.boolean.opBoolean","INTERSECT",EDGE,{"derivedFrom":[makeQuery(id+"F1.opExtrude","SWEPT_FACE",FACE,{"disambiguationData":[OSD([sQuery(id+"F0.wireOp",EDGE,"E5.5.0")])]}),makeQuery(id+"F10.opRevolve","SWEPT_FACE",FACE,{"disambiguationData":[OSD([sQuery(id+"F9.wireOp",EDGE,"E14")])]})]});
            var Q17;
            Q17=makeQuery(id+"F10.boolean.opBoolean","INTERSECT",EDGE,{"derivedFrom":[makeQuery(id+"F1.opExtrude","SWEPT_FACE",FACE,{"disambiguationData":[OSD([sQuery(id+"F0.wireOp",EDGE,"E6.6.6.0")])]}),makeQuery(id+"F10.opRevolve","SWEPT_FACE",FACE,{"disambiguationData":[OSD([sQuery(id+"F9.wireOp",EDGE,"E14")])]})]});
            var Q18;
            Q18=makeQuery(id+"F10.boolean.opBoolean","INTERSECT",EDGE,{"derivedFrom":[makeQuery(id+"F1.opExtrude","SWEPT_FACE",FACE,{"disambiguationData":[OSD([sQuery(id+"F0.wireOp",EDGE,"E5.4.0")])]}),makeQuery(id+"F10.opRevolve","SWEPT_FACE",FACE,{"disambiguationData":[OSD([sQuery(id+"F9.wireOp",EDGE,"E14")])]})]});
            var Q19;
            Q19=makeQuery(id+"F10.boolean.opBoolean","INTERSECT",EDGE,{"derivedFrom":[makeQuery(id+"F1.opExtrude","SWEPT_FACE",FACE,{"disambiguationData":[OSD([sQuery(id+"F0.wireOp",EDGE,"E5.4.2")])]}),makeQuery(id+"F10.opRevolve","SWEPT_FACE",FACE,{"disambiguationData":[OSD([sQuery(id+"F9.wireOp",EDGE,"E14")])]})]});
            fillet(context, id + "F13", {"entities" : qUnion([Q0, Q1, Q2, Q3, Q4, Q5, Q6, Q7, Q8, Q9, Q10, Q11, Q12, Q13, Q14, Q15, Q16, Q17, Q18, Q19]), "radius" : 7.62 * mm, "tangentPropagation" : true, "allowEdgeOverflow" : false});
        }
        {
            var Q0;
            Q0=makeQuery(id+"F10.boolean.opBoolean","MERGE",FACE,{"derivedFrom":[makeQuery(id+"F1.opExtrude","CAP_FACE",FACE,{"disambiguationData":[OSD([sQuery(id+"F0.wireOp",EDGE,"E0"),sQuery(id+"F0.wireOp",EDGE,"E1"),sQuery(id+"F0.wireOp",EDGE,"E3"),sQuery(id+"F0.wireOp",EDGE,"E4"),sQuery(id+"F0.wireOp",EDGE,"E5.1.0"),sQuery(id+"F0.wireOp",EDGE,"E5.1.1"),sQuery(id+"F0.wireOp",EDGE,"E5.1.2"),sQuery(id+"F0.wireOp",EDGE,"E5.2.0"),sQuery(id+"F0.wireOp",EDGE,"E5.2.1"),sQuery(id+"F0.wireOp",EDGE,"E5.2.2"),sQuery(id+"F0.wireOp",EDGE,"E5.3.0"),sQuery(id+"F0.wireOp",EDGE,"E5.3.1"),sQuery(id+"F0.wireOp",EDGE,"E5.3.2"),sQuery(id+"F0.wireOp",EDGE,"E5.4.0"),sQuery(id+"F0.wireOp",EDGE,"E5.4.1"),sQuery(id+"F0.wireOp",EDGE,"E5.4.2"),sQuery(id+"F0.wireOp",EDGE,"E5.5.0"),sQuery(id+"F0.wireOp",EDGE,"E5.5.1"),sQuery(id+"F0.wireOp",EDGE,"E5.5.2"),sQuery(id+"F0.wireOp",EDGE,"E6.1.6.0"),sQuery(id+"F0.wireOp",EDGE,"E6.3.6.0"),sQuery(id+"F0.wireOp",EDGE,"E6.6.6.0"),sQuery(id+"F0.wireOp",EDGE,"E6.1.7.0"),sQuery(id+"F0.wireOp",EDGE,"E6.3.7.0"),sQuery(id+"F0.wireOp",EDGE,"E6.6.7.0"),sQuery(id+"F0.wireOp",EDGE,"E6.1.8.0"),sQuery(id+"F0.wireOp",EDGE,"E6.3.8.0"),sQuery(id+"F0.wireOp",EDGE,"E6.6.8.0"),sQuery(id+"F0.wireOp",EDGE,"E6.1.9.0"),sQuery(id+"F0.wireOp",EDGE,"E6.3.9.0"),sQuery(id+"F0.wireOp",EDGE,"E6.6.9.0"),sQuery(id+"F0.wireOp",EDGE,"E7")])],"isStart":false}),makeQuery(id+"F10.opRevolve","SWEPT_FACE",FACE,{"disambiguationData":[OSD([sQuery(id+"F9.wireOp",EDGE,"E12.0.2")])]})]});
            extrude(context, id + "F14", {"entities" : qUnion([Q0]), "operationType" : NewBodyOperationType.ADD, "depth" : 25.4 * mm, "offsetDistance" : 25.4 * mm});
        }
    });
